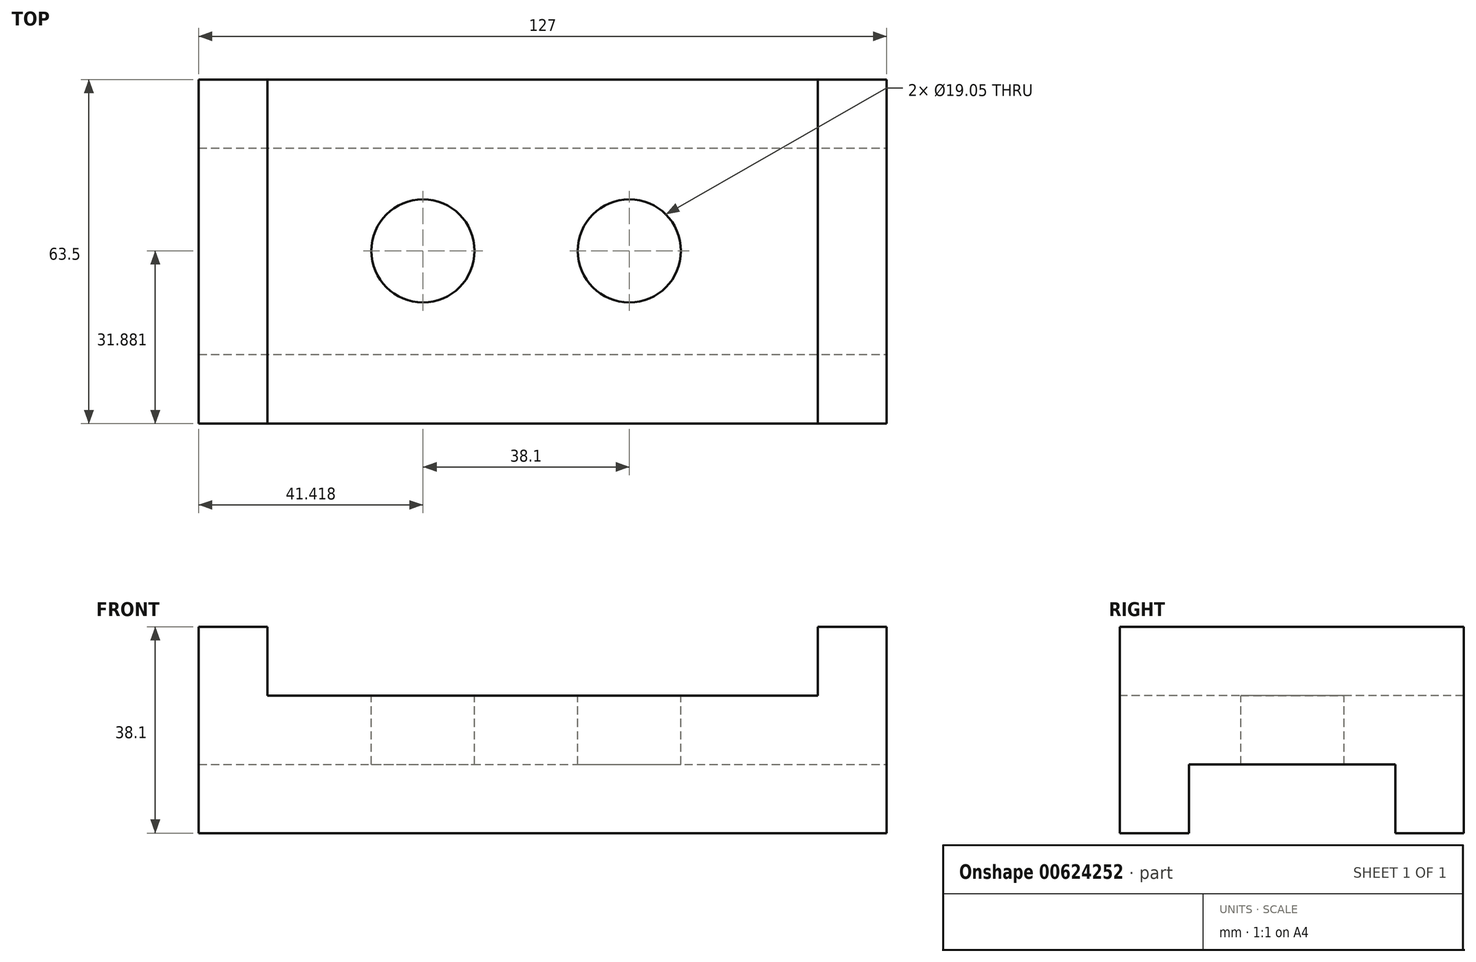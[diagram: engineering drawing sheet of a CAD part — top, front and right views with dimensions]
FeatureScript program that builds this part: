
annotation { "Feature Type Name" : "Feature", "Feature Type Description" : "" }
export const myFeature = defineFeature(function(context is Context, id is Id, definition is map)
    precondition{}
    {
        {
            var Q0;
            Q0=qCreatedBy(makeId("Top.planeOp"),FACE);
            var sketch = newSketch(context, id + "F0", { "sketchPlane" : qUnion([Q0])});
            skLineSegment(sketch, "E0.bottom", {"start": v(-76.97, 4.13) * mm, "end": v(50.03, 4.13) * mm});
            skLineSegment(sketch, "E0.top", {"start": v(-76.97, -59.37) * mm, "end": v(50.03, -59.37) * mm});
            skLineSegment(sketch, "E0.left", {"start": v(-76.97, 4.13) * mm, "end": v(-76.97, -59.37) * mm});
            skLineSegment(sketch, "E0.right", {"start": v(50.03, 4.13) * mm, "end": v(50.03, -59.37) * mm});
            skSolve(sketch);
        }
        {
            var Q0;
            Q0 = qSketchRegion(id + "F0", true);
            extrude(context, id + "F1", {"entities" : qUnion([Q0]), "depth" : 38.1 * mm, "offsetDistance" : 25.4 * mm});
        }
        {
            var Q0;
            Q0=makeQuery(id+"F1.opExtrude","SWEPT_FACE",FACE,{"disambiguationData":[OSD([sQuery(id+"F0.wireOp",EDGE,"E0.top")])]});
            var sketch = newSketch(context, id + "F2", { "sketchPlane" : qUnion([Q0])});
            skLineSegment(sketch, "E1", {"start": v(-64.27, 38.1) * mm, "end": v(-64.27, 25.4) * mm});
            skLineSegment(sketch, "E2", {"start": v(-64.27, 25.4) * mm, "end": v(37.33, 25.4) * mm});
            skLineSegment(sketch, "E3", {"start": v(37.33, 25.4) * mm, "end": v(37.33, 38.1) * mm});
            skSolve(sketch);
        }
        {
            var Q0;
            Q0 = qSketchRegion(id + "F2", true);
            var Q1;
            {var subQ0=sQuery(id+"F2.wireOp",EDGE,"E1");Q1=makeQuery(id+"F2.imprint","IMPRINT",FACE,{"disambiguationData":[TD([[makeQuery(id+"F2.imprint","IMPRINT",EDGE,{"derivedFrom":subQ0}),1.0]])]});}
            extrude(context, id + "F3", {"entities" : qUnion([Q0, Q1]), "operationType" : NewBodyOperationType.REMOVE, "endBound" : BoundingType.UP_TO_NEXT, "oppositeDirection" : true, "depth" : 25.4 * mm, "offsetDistance" : 25.4 * mm});
        }
        {
            var Q0;
            Q0=makeQuery(id+"F1.opExtrude","SWEPT_FACE",FACE,{"disambiguationData":[OSD([sQuery(id+"F0.wireOp",EDGE,"E0.right")])]});
            var sketch = newSketch(context, id + "F4", { "sketchPlane" : qUnion([Q0])});
            skLineSegment(sketch, "E4", {"start": v(-59.37, 0) * mm, "end": v(-46.6, 0) * mm});
            skLineSegment(sketch, "E5", {"start": v(-46.6, 0) * mm, "end": v(-46.6, 12.7) * mm});
            skLineSegment(sketch, "E6", {"start": v(-46.6, 12.7) * mm, "end": v(-8.5, 12.7) * mm});
            skLineSegment(sketch, "E7", {"start": v(-8.5, 12.7) * mm, "end": v(-8.5, 0) * mm});
            skLineSegment(sketch, "E8", {"start": v(-8.5, 0) * mm, "end": v(4.13, 0) * mm});
            skSolve(sketch);
        }
        {
            var Q0;
            {var subQ0=sQuery(id+"F4.wireOp",EDGE,"E5");Q0=makeQuery(id+"F4.imprint","IMPRINT",FACE,{"disambiguationData":[TD([[makeQuery(id+"F4.imprint","IMPRINT",EDGE,{"derivedFrom":subQ0}),-1.0]])]});}
            extrude(context, id + "F5", {"entities" : qUnion([Q0]), "operationType" : NewBodyOperationType.REMOVE, "endBound" : BoundingType.THROUGH_ALL, "oppositeDirection" : true, "depth" : 76.45 * mm, "offsetDistance" : 25.4 * mm});
        }
        {
            var Q0;
            Q0=makeQuery(id+"F3.boolean.opBoolean","COPY",FACE,{"derivedFrom":makeQuery(id+"F3.opExtrude","SWEPT_FACE",FACE,{"disambiguationData":[OSD([sQuery(id+"F2.wireOp",EDGE,"E2")])]})});
            var sketch = newSketch(context, id + "F6", { "sketchPlane" : qUnion([Q0])});
            skCircle(sketch, "E9", {"center": v(-35.55, -27.49) * mm, "radius": 9.53 * mm});
            skLineSegment(sketch, "E10", {"start": v(-35.55, -27.49) * mm, "end": v(2.55, -27.49) * mm});
            skCircle(sketch, "E11", {"center": v(2.55, -27.49) * mm, "radius": 9.53 * mm});
            skSolve(sketch);
        }
        {
            var Q0;
            Q0=sQuery(id+"F6.wireOp",VERTEX,"E10.start");
            var Q1;
            Q1=sQuery(id+"F6.wireOp",VERTEX,"E11.center");
            var Q2;
            Q2=makeQuery(id+"F1.opExtrude","SWEPT_BODY",BODY,{"disambiguationData":[OSD([sQuery(id+"F0.wireOp",EDGE,"E0.bottom"),sQuery(id+"F0.wireOp",EDGE,"E0.top"),sQuery(id+"F0.wireOp",EDGE,"E0.left"),sQuery(id+"F0.wireOp",EDGE,"E0.right")])]});
            hole(context, id + "F7", {"style" : HoleStyle.SIMPLE, "endStyle" : HoleEndStyle.THROUGH, "holeDiameter" : 19.05 * mm, "majorDiameter" : 6.35 * mm, "isTappedThrough" : true, "tappedDepth" : 12.7 * mm, "tapClearance" : 3, "locations" : qUnion([Q0, Q1]), "scope" : qUnion([Q2])});
        }
    });
